# Revit family: LAC-Dahlia
name_source: partatom
category: Lighting Fixtures
revit_build: Autodesk Revit 2014 (Build: 20130709_2115(x64)
units: mm (PartAtom-declared; Revit-internal decimal feet)

## types (2) — shared parameters
Color Filter = 16777215
Comments = This model is for use in spatial massing and rendering. Please contact LightArt for pick-point placement and installation details.
Dimming Compatibility = Option available
Dimming Lamp Color Temperature Shift = <None>
Driver = 24v
Emit from Line Length = 1' - 0"
HARDWARE = Matte silver canopy mounts to round
junction box (provided by others)
(4) stainless steel cables to ceiling
Silver power cord to canopy
Adjustable 12”-96” suspension
Hardware = Stainless Steel Cables
Height From Face = 5' - 0"
Input = 120v-277v
LIGHTING = (1) 14W E26 Base CFL Globe
3500K 82 CRI light source
277V option available
LED option available
GU24 base option available
Dimming option available
UL Labeled
Light Source Symbol Size = 0' - 10"
Manufacturer = LightArt
Model = LAC-Dahlia
STANDARDS = Customizable dimensions, materials,
hardware and lighting
4-6 week lead time
10,000+ 3form material options
1 year limited warranty
Pricing based on maximum sheet yield and
PGB material
Contact for custom pricing
Shade = Shade

## per-type parameters (varying)
| type | A | B |
| 23"Dia. x 14"H (style a) | Yes | No |
| 23"Dia. x 14"H (style b) | No | Yes |

## geometry (parser evidence)
native form markers: Sweep x48
no freeform markers — native parametric forms only
